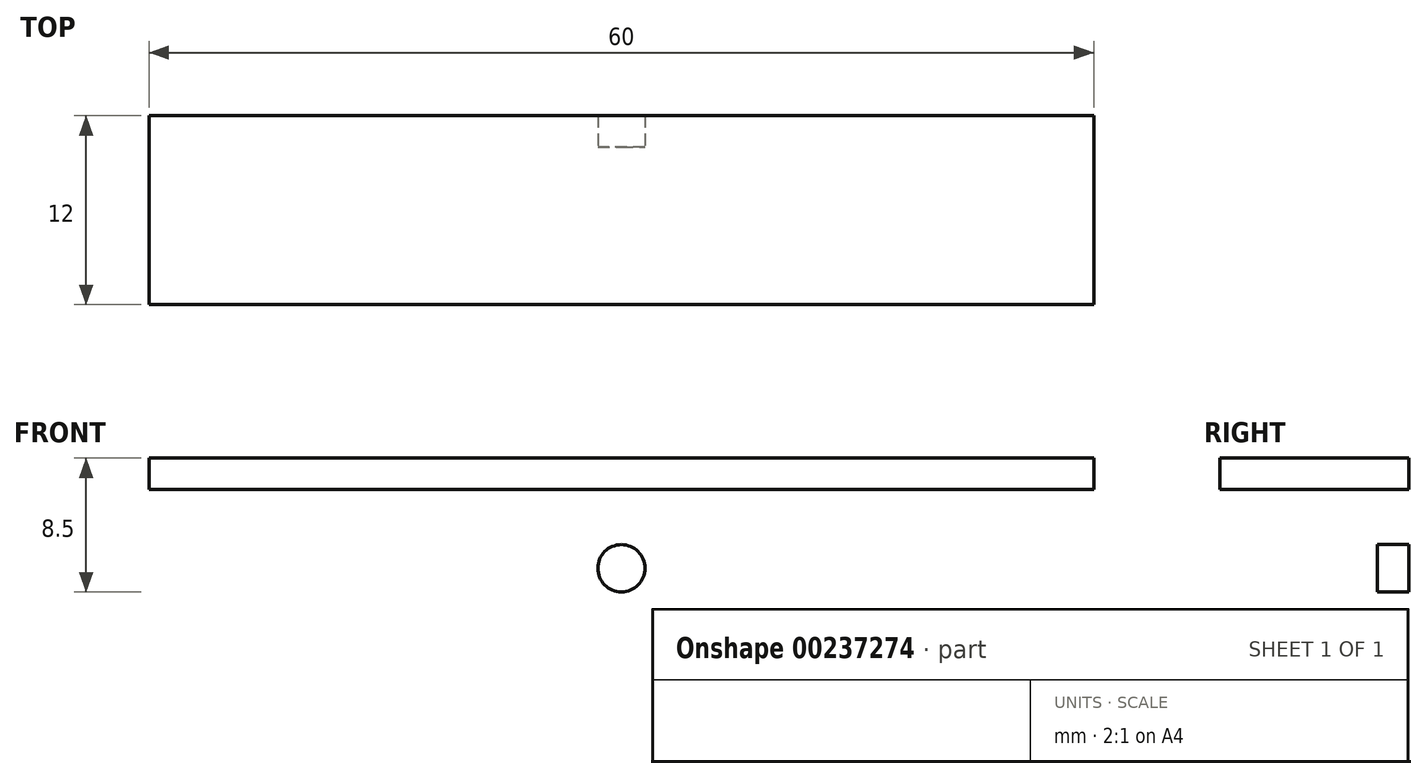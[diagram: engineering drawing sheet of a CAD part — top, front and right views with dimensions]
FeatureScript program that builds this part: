
annotation { "Feature Type Name" : "Feature", "Feature Type Description" : "" }
export const myFeature = defineFeature(function(context is Context, id is Id, definition is map)
    precondition{}
    {
        {
            var Q0;
            Q0=qCreatedBy(makeId("Front.planeOp"),FACE);
            var sketch = newSketch(context, id + "F0", { "sketchPlane" : qUnion([Q0])});
            skLineSegment(sketch, "E0.bottom", {"start": v(-30, 15) * mm, "end": v(30, 15) * mm});
            skLineSegment(sketch, "E0.top", {"start": v(-30, -15) * mm, "end": v(30, -15) * mm});
            skLineSegment(sketch, "E0.left", {"start": v(-30, 15) * mm, "end": v(-30, -15) * mm});
            skLineSegment(sketch, "E0.right", {"start": v(30, 15) * mm, "end": v(30, -15) * mm});
            skPoint(sketch, "E0.middle", {"position": v(0, 0) * mm});
            skSolve(sketch);
        }
        {
            var Q0;
            Q0=makeQuery(id+"F0.imprint","IMPRINT",FACE,{"disambiguationData":[TD([[makeQuery(id+"F0.imprint","IMPRINT",EDGE,{"derivedFrom":sQuery(id+"F0.wireOp",EDGE,"E0.bottom")}),-1.0]])]});
            extrude(context, id + "F1", {"entities" : qUnion([Q0]), "depth" : 2 * mm});
        }
        {
            var Q0;
            Q0=makeQuery(id+"F1.opExtrude","CAP_FACE",FACE,{"disambiguationData":[OSD([sQuery(id+"F0.wireOp",EDGE,"E0.bottom"),sQuery(id+"F0.wireOp",EDGE,"E0.top"),sQuery(id+"F0.wireOp",EDGE,"E0.left"),sQuery(id+"F0.wireOp",EDGE,"E0.right"),sQuery(id+"F0.wireOp",EDGE,"etlL4guk-orcU-iKfM-RefP-JZowgscgbXgj")])],"isStart":false});
            var sketch = newSketch(context, id + "F2", { "sketchPlane" : qUnion([Q0])});
            skLineSegment(sketch, "E1.bottom", {"start": v(-30, 15) * mm, "end": v(30, 15) * mm});
            skLineSegment(sketch, "E1.top", {"start": v(-30, 13) * mm, "end": v(30, 13) * mm});
            skLineSegment(sketch, "E1.left", {"start": v(-30, 15) * mm, "end": v(-30, 13) * mm});
            skLineSegment(sketch, "E1.right", {"start": v(30, 15) * mm, "end": v(30, 13) * mm});
            skSolve(sketch);
        }
        {
            var Q0;
            Q0 = qSketchRegion(id + "F2", true);
            extrude(context, id + "F3", {"entities" : qUnion([Q0]), "operationType" : NewBodyOperationType.ADD, "depth" : 10 * mm});
        }
        {
            var Q0;
            Q0=makeQuery(id+"F1.opExtrude","CAP_FACE",FACE,{"disambiguationData":[OSD([sQuery(id+"F0.wireOp",EDGE,"E0.bottom"),sQuery(id+"F0.wireOp",EDGE,"E0.top"),sQuery(id+"F0.wireOp",EDGE,"E0.left"),sQuery(id+"F0.wireOp",EDGE,"E0.right"),sQuery(id+"F0.wireOp",EDGE,"etlL4guk-orcU-iKfM-RefP-JZowgscgbXgj")])],"isStart":false});
            var sketch = newSketch(context, id + "F4", { "sketchPlane" : qUnion([Q0])});
            skLineSegment(sketch, "E2", {"start": v(-30, 8) * mm, "end": v(30, 8) * mm});
            skLineSegment(sketch, "E3.bottom", {"start": v(-26, 9) * mm, "end": v(-15, 9) * mm});
            skLineSegment(sketch, "E3.top", {"start": v(-26, 7) * mm, "end": v(-15, 7) * mm});
            skLineSegment(sketch, "E3.left", {"start": v(-26, 9) * mm, "end": v(-26, 7) * mm});
            skLineSegment(sketch, "E3.right", {"start": v(-15, 9) * mm, "end": v(-15, 7) * mm});
            skPoint(sketch, "E3.middle", {"position": v(-20.5, 8) * mm});
            skLineSegment(sketch, "E4.bottom", {"start": v(15, 9) * mm, "end": v(26, 9) * mm});
            skLineSegment(sketch, "E4.top", {"start": v(15, 7) * mm, "end": v(26, 7) * mm});
            skLineSegment(sketch, "E4.left", {"start": v(15, 9) * mm, "end": v(15, 7) * mm});
            skLineSegment(sketch, "E4.right", {"start": v(26, 9) * mm, "end": v(26, 7) * mm});
            skPoint(sketch, "E4.middle", {"position": v(20.5, 8) * mm});
            skCircle(sketch, "E5", {"center": v(0, 8) * mm, "radius": 1.5 * mm});
            skSolve(sketch);
        }
        {
            var Q0;
            {var subQ5=sQuery(id+"F4.wireOp",EDGE,"E4.bottom");Q0=makeQuery(id+"F4.imprint","IMPRINT",FACE,{"disambiguationData":[TD([[makeQuery(id+"F4.imprint","IMPRINT",EDGE,{"derivedFrom":subQ5}),-1.0]])]});}
            var Q1;
            {var subQ5=sQuery(id+"F4.wireOp",EDGE,"E4.top");Q1=makeQuery(id+"F4.imprint","IMPRINT",FACE,{"disambiguationData":[TD([[makeQuery(id+"F4.imprint","IMPRINT",EDGE,{"derivedFrom":subQ5}),1.0]])]});}
            var Q2;
            {var subQ0=sQuery(id+"F4.wireOp",EDGE,"E5");var subQ1=sQuery(id+"F4.wireOp",EDGE,"E2");var subQ2=makeQuery(id+"F4.imprint","INTERSECT",VERTEX,{"disambiguationData":[OD(0.0)],"derivedFrom":[subQ1,subQ0]});Q2=makeQuery(id+"F4.imprint","IMPRINT",FACE,{"disambiguationData":[TD([[makeQuery(id+"F4.imprint","IMPRINT",EDGE,{"disambiguationData":[TD([[subQ2,-1.0]])],"derivedFrom":subQ1}),-1.0]])]});}
            var Q3;
            {var subQ0=sQuery(id+"F4.wireOp",EDGE,"E5");var subQ1=sQuery(id+"F4.wireOp",EDGE,"E2");var subQ2=makeQuery(id+"F4.imprint","INTERSECT",VERTEX,{"disambiguationData":[OD(0.0)],"derivedFrom":[subQ1,subQ0]});Q3=makeQuery(id+"F4.imprint","IMPRINT",FACE,{"disambiguationData":[TD([[makeQuery(id+"F4.imprint","IMPRINT",EDGE,{"disambiguationData":[TD([[subQ2,-1.0]])],"derivedFrom":subQ1}),1.0]])]});}
            var Q4;
            {var subQ5=sQuery(id+"F4.wireOp",EDGE,"E3.bottom");Q4=makeQuery(id+"F4.imprint","IMPRINT",FACE,{"disambiguationData":[TD([[makeQuery(id+"F4.imprint","IMPRINT",EDGE,{"derivedFrom":subQ5}),-1.0]])]});}
            var Q5;
            {var subQ5=sQuery(id+"F4.wireOp",EDGE,"E3.top");Q5=makeQuery(id+"F4.imprint","IMPRINT",FACE,{"disambiguationData":[TD([[makeQuery(id+"F4.imprint","IMPRINT",EDGE,{"derivedFrom":subQ5}),1.0]])]});}
            extrude(context, id + "F5", {"entities" : qUnion([Q0, Q1, Q2, Q3, Q4, Q5]), "operationType" : NewBodyOperationType.REMOVE, "oppositeDirection" : true, "depth" : 3 * mm});
        }
        {
            var Q0;
            Q0=makeQuery(id+"F1.opExtrude","CAP_FACE",FACE,{"disambiguationData":[OSD([sQuery(id+"F0.wireOp",EDGE,"E0.bottom"),sQuery(id+"F0.wireOp",EDGE,"E0.top"),sQuery(id+"F0.wireOp",EDGE,"E0.left"),sQuery(id+"F0.wireOp",EDGE,"E0.right"),sQuery(id+"F0.wireOp",EDGE,"etlL4guk-orcU-iKfM-RefP-JZowgscgbXgj")])],"isStart":false});
            var sketch = newSketch(context, id + "F6", { "sketchPlane" : qUnion([Q0])});
            skLineSegment(sketch, "E6", {"start": v(-30, 3) * mm, "end": v(30, 3) * mm});
            skLineSegment(sketch, "E7.bottom", {"start": v(-26.03, 4) * mm, "end": v(-15.03, 4) * mm});
            skLineSegment(sketch, "E7.top", {"start": v(-26.03, 2) * mm, "end": v(-15.03, 2) * mm});
            skLineSegment(sketch, "E7.left", {"start": v(-26.03, 4) * mm, "end": v(-26.03, 2) * mm});
            skLineSegment(sketch, "E7.right", {"start": v(-15.03, 4) * mm, "end": v(-15.03, 2) * mm});
            skPoint(sketch, "E7.middle", {"position": v(-20.53, 3) * mm});
            skLineSegment(sketch, "E8.bottom", {"start": v(15.03, 4) * mm, "end": v(26.03, 4) * mm});
            skLineSegment(sketch, "E8.top", {"start": v(15.03, 2) * mm, "end": v(26.03, 2) * mm});
            skLineSegment(sketch, "E8.left", {"start": v(15.03, 4) * mm, "end": v(15.03, 2) * mm});
            skLineSegment(sketch, "E8.right", {"start": v(26.03, 4) * mm, "end": v(26.03, 2) * mm});
            skPoint(sketch, "E8.middle", {"position": v(20.53, 3) * mm});
            skCircle(sketch, "E9", {"center": v(0, 3) * mm, "radius": 1.5 * mm});
            skSolve(sketch);
        }
        {
            var Q0;
            Q0 = qSketchRegion(id + "F6", true);
            extrude(context, id + "F7", {"entities" : qUnion([Q0]), "operationType" : NewBodyOperationType.REMOVE, "oppositeDirection" : true, "depth" : 25 * mm});
        }
        {
            var Q0;
            Q0=makeQuery(id+"F1.opExtrude","CAP_FACE",FACE,{"disambiguationData":[OSD([sQuery(id+"F0.wireOp",EDGE,"E0.bottom"),sQuery(id+"F0.wireOp",EDGE,"E0.top"),sQuery(id+"F0.wireOp",EDGE,"E0.left"),sQuery(id+"F0.wireOp",EDGE,"E0.right")])],"isStart":false});
            var sketch = newSketch(context, id + "F8", { "sketchPlane" : qUnion([Q0])});
            skLineSegment(sketch, "E10", {"start": v(-30, -2) * mm, "end": v(30, -2) * mm});
            skLineSegment(sketch, "E11.bottom", {"start": v(-26.03, -1) * mm, "end": v(-15.03, -1) * mm});
            skLineSegment(sketch, "E11.top", {"start": v(-26.03, -3) * mm, "end": v(-15.03, -3) * mm});
            skLineSegment(sketch, "E11.left", {"start": v(-26.03, -1) * mm, "end": v(-26.03, -3) * mm});
            skLineSegment(sketch, "E11.right", {"start": v(-15.03, -1) * mm, "end": v(-15.03, -3) * mm});
            skPoint(sketch, "E11.middle", {"position": v(-20.53, -2) * mm});
            skLineSegment(sketch, "E12.bottom", {"start": v(15.03, -1) * mm, "end": v(26.03, -1) * mm});
            skLineSegment(sketch, "E12.top", {"start": v(15.03, -3) * mm, "end": v(26.03, -3) * mm});
            skLineSegment(sketch, "E12.left", {"start": v(15.03, -1) * mm, "end": v(15.03, -3) * mm});
            skLineSegment(sketch, "E12.right", {"start": v(26.03, -1) * mm, "end": v(26.03, -3) * mm});
            skPoint(sketch, "E12.middle", {"position": v(20.53, -2) * mm});
            skCircle(sketch, "E13", {"center": v(0, -2) * mm, "radius": 1.5 * mm});
            skSolve(sketch);
        }
        {
            var Q0;
            Q0 = qSketchRegion(id + "F8", true);
            extrude(context, id + "F9", {"entities" : qUnion([Q0]), "operationType" : NewBodyOperationType.REMOVE, "oppositeDirection" : true, "depth" : 25 * mm});
        }
        {
            var Q0;
            Q0=makeQuery(id+"F1.opExtrude","CAP_FACE",FACE,{"disambiguationData":[OSD([sQuery(id+"F0.wireOp",EDGE,"E0.bottom"),sQuery(id+"F0.wireOp",EDGE,"E0.top"),sQuery(id+"F0.wireOp",EDGE,"E0.left"),sQuery(id+"F0.wireOp",EDGE,"E0.right")])],"isStart":false});
            var sketch = newSketch(context, id + "F10", { "sketchPlane" : qUnion([Q0])});
            skLineSegment(sketch, "E14", {"start": v(-30, -7) * mm, "end": v(30, -7) * mm});
            skLineSegment(sketch, "E15.bottom", {"start": v(-26.03, -6) * mm, "end": v(-15.03, -6) * mm});
            skLineSegment(sketch, "E15.top", {"start": v(-26.03, -8) * mm, "end": v(-15.03, -8) * mm});
            skLineSegment(sketch, "E15.left", {"start": v(-26.03, -6) * mm, "end": v(-26.03, -8) * mm});
            skLineSegment(sketch, "E15.right", {"start": v(-15.03, -6) * mm, "end": v(-15.03, -8) * mm});
            skPoint(sketch, "E15.middle", {"position": v(-20.53, -7) * mm});
            skLineSegment(sketch, "E16.bottom", {"start": v(15.03, -6) * mm, "end": v(26.03, -6) * mm});
            skLineSegment(sketch, "E16.top", {"start": v(15.03, -8) * mm, "end": v(26.03, -8) * mm});
            skLineSegment(sketch, "E16.left", {"start": v(15.03, -6) * mm, "end": v(15.03, -8) * mm});
            skLineSegment(sketch, "E16.right", {"start": v(26.03, -6) * mm, "end": v(26.03, -8) * mm});
            skPoint(sketch, "E16.middle", {"position": v(20.53, -7) * mm});
            skCircle(sketch, "E17", {"center": v(0, -7) * mm, "radius": 1.5 * mm});
            skSolve(sketch);
        }
        {
            var Q0;
            Q0 = qSketchRegion(id + "F10", true);
            extrude(context, id + "F11", {"entities" : qUnion([Q0]), "operationType" : NewBodyOperationType.REMOVE, "oppositeDirection" : true, "depth" : 25 * mm});
        }
        {
            var Q0;
            Q0=makeQuery(id+"F1.opExtrude","CAP_FACE",FACE,{"disambiguationData":[OSD([sQuery(id+"F0.wireOp",EDGE,"E0.bottom"),sQuery(id+"F0.wireOp",EDGE,"E0.top"),sQuery(id+"F0.wireOp",EDGE,"E0.left"),sQuery(id+"F0.wireOp",EDGE,"E0.right")])],"isStart":false});
            var sketch = newSketch(context, id + "F12", { "sketchPlane" : qUnion([Q0])});
            skLineSegment(sketch, "E18", {"start": v(-30, -12) * mm, "end": v(30, -12) * mm});
            skLineSegment(sketch, "E19.bottom", {"start": v(-26.03, -11) * mm, "end": v(-15.03, -11) * mm});
            skLineSegment(sketch, "E19.top", {"start": v(-26.03, -13) * mm, "end": v(-15.03, -13) * mm});
            skLineSegment(sketch, "E19.left", {"start": v(-26.03, -11) * mm, "end": v(-26.03, -13) * mm});
            skLineSegment(sketch, "E19.right", {"start": v(-15.03, -11) * mm, "end": v(-15.03, -13) * mm});
            skPoint(sketch, "E19.middle", {"position": v(-20.53, -12) * mm});
            skLineSegment(sketch, "E20.bottom", {"start": v(15.03, -11) * mm, "end": v(26.03, -11) * mm});
            skLineSegment(sketch, "E20.top", {"start": v(15.03, -13) * mm, "end": v(26.03, -13) * mm});
            skLineSegment(sketch, "E20.left", {"start": v(15.03, -11) * mm, "end": v(15.03, -13) * mm});
            skLineSegment(sketch, "E20.right", {"start": v(26.03, -11) * mm, "end": v(26.03, -13) * mm});
            skPoint(sketch, "E20.middle", {"position": v(20.53, -12) * mm});
            skCircle(sketch, "E21", {"center": v(0, -12) * mm, "radius": 1.5 * mm});
            skSolve(sketch);
        }
        {
            var Q0;
            Q0 = qSketchRegion(id + "F12", true);
            extrude(context, id + "F13", {"entities" : qUnion([Q0]), "operationType" : NewBodyOperationType.REMOVE, "oppositeDirection" : true, "depth" : 25 * mm});
        }
        {
            var Q0;
            Q0=makeQuery(id+"F1.opExtrude","CAP_FACE",FACE,{"disambiguationData":[OSD([sQuery(id+"F0.wireOp",EDGE,"E0.bottom"),sQuery(id+"F0.wireOp",EDGE,"E0.top"),sQuery(id+"F0.wireOp",EDGE,"E0.left"),sQuery(id+"F0.wireOp",EDGE,"E0.right")])],"isStart":false});
            var sketch = newSketch(context, id + "F14", { "sketchPlane" : qUnion([Q0])});
            skText(sketch, "E22", { "text": "5", "fontName": "OpenSans-Bold.ttf"});
            const initialGuessF14  = {"E22": [0.00423, 0.00641, 1, 0, 0.00403]};
            skSetInitialGuess(sketch, initialGuessF14);
            skSolve(sketch);
        }
        {
            var Q0;
            Q0 = qSketchRegion(id + "F14", true);
            extrude(context, id + "F15", {"entities" : qUnion([Q0]), "operationType" : NewBodyOperationType.REMOVE, "oppositeDirection" : true, "depth" : 1 * mm});
        }
        {
            var Q0;
            Q0=makeQuery(id+"F1.opExtrude","CAP_FACE",FACE,{"disambiguationData":[OSD([sQuery(id+"F0.wireOp",EDGE,"E0.bottom"),sQuery(id+"F0.wireOp",EDGE,"E0.top"),sQuery(id+"F0.wireOp",EDGE,"E0.left"),sQuery(id+"F0.wireOp",EDGE,"E0.right")])],"isStart":false});
            var sketch = newSketch(context, id + "F16", { "sketchPlane" : qUnion([Q0])});
            skText(sketch, "E23", { "text": "10", "fontName": "OpenSans-Bold.ttf"});
            const initialGuessF16  = {"E23": [-0.01024, 0.00126, 1, 0, 0.00348]};
            skSetInitialGuess(sketch, initialGuessF16);
            skSolve(sketch);
        }
        {
            var Q0;
            Q0 = qSketchRegion(id + "F16", true);
            extrude(context, id + "F17", {"entities" : qUnion([Q0]), "operationType" : NewBodyOperationType.REMOVE, "oppositeDirection" : true, "depth" : 1 * mm});
        }
        {
            var Q0;
            {var subQ0=sQuery(id+"F0.wireOp",EDGE,"E0.left");var subQ1=sQuery(id+"F0.wireOp",EDGE,"E0.top");var subQ2=sQuery(id+"F0.wireOp",EDGE,"E0.right");Q0=makeQuery(id+"F17.boolean.opBoolean","SPLIT",FACE,{"disambiguationData":[TD([makeQuery(id+"F1.opExtrude","SWEPT_FACE",FACE,{"disambiguationData":[OSD([subQ1])]})])],"derivedFrom":makeQuery(id+"F1.opExtrude","CAP_FACE",FACE,{"disambiguationData":[OSD([sQuery(id+"F0.wireOp",EDGE,"E0.bottom"),subQ1,subQ0,subQ2])],"isStart":false})});}
            var sketch = newSketch(context, id + "F18", { "sketchPlane" : qUnion([Q0])});
            skText(sketch, "E24", { "text": "15", "fontName": "OpenSans-Bold.ttf"});
            const initialGuessF18  = {"E24": [0.0052, -0.0036, 1, 0, 0.0036]};
            skSetInitialGuess(sketch, initialGuessF18);
            skSolve(sketch);
        }
        {
            var Q0;
            Q0 = qSketchRegion(id + "F18", true);
            extrude(context, id + "F19", {"entities" : qUnion([Q0]), "operationType" : NewBodyOperationType.REMOVE, "oppositeDirection" : true, "depth" : 1 * mm});
        }
        {
            var Q0;
            {var subQ0=sQuery(id+"F0.wireOp",EDGE,"E0.left");var subQ1=sQuery(id+"F0.wireOp",EDGE,"E0.top");var subQ2=sQuery(id+"F0.wireOp",EDGE,"E0.right");Q0=makeQuery(id+"F17.boolean.opBoolean","SPLIT",FACE,{"disambiguationData":[TD([makeQuery(id+"F1.opExtrude","SWEPT_FACE",FACE,{"disambiguationData":[OSD([subQ1])]})])],"derivedFrom":makeQuery(id+"F1.opExtrude","CAP_FACE",FACE,{"disambiguationData":[OSD([sQuery(id+"F0.wireOp",EDGE,"E0.bottom"),subQ1,subQ0,subQ2])],"isStart":false})});}
            var sketch = newSketch(context, id + "F20", { "sketchPlane" : qUnion([Q0])});
            skText(sketch, "E25", { "text": "20", "fontName": "OpenSans-Bold.ttf"});
            const initialGuessF20  = {"E25": [-0.0101, -0.00875, 1, 0, 0.0039]};
            skSetInitialGuess(sketch, initialGuessF20);
            skSolve(sketch);
        }
        {
            var Q0;
            Q0 = qSketchRegion(id + "F20", true);
            extrude(context, id + "F21", {"entities" : qUnion([Q0]), "operationType" : NewBodyOperationType.REMOVE, "oppositeDirection" : true, "depth" : 1 * mm});
        }
        {
            var Q0;
            {var subQ54=sQuery(id+"F0.wireOp",EDGE,"E0.right");var subQ63=sQuery(id+"F0.wireOp",EDGE,"E0.top");var subQ64=makeQuery(id+"F1.opExtrude","SWEPT_FACE",FACE,{"disambiguationData":[OSD([subQ63])]});var subQ67=sQuery(id+"F0.wireOp",EDGE,"E0.left");Q0=makeQuery(id+"F21.boolean.opBoolean","SPLIT",FACE,{"disambiguationData":[TD([subQ64])],"derivedFrom":makeQuery(id+"F17.boolean.opBoolean","SPLIT",FACE,{"disambiguationData":[TD([subQ64])],"derivedFrom":makeQuery(id+"F1.opExtrude","CAP_FACE",FACE,{"disambiguationData":[OSD([sQuery(id+"F0.wireOp",EDGE,"E0.bottom"),subQ63,subQ67,subQ54])],"isStart":false})})});}
            var sketch = newSketch(context, id + "F22", { "sketchPlane" : qUnion([Q0])});
            skText(sketch, "E26", { "text": "25", "fontName": "OpenSans-Bold.ttf"});
            const initialGuessF22  = {"E26": [0.00576, -0.0132, 1, 0, 0.00348]};
            skSetInitialGuess(sketch, initialGuessF22);
            skSolve(sketch);
        }
        {
            var Q0;
            Q0 = qSketchRegion(id + "F22", true);
            extrude(context, id + "F23", {"entities" : qUnion([Q0]), "operationType" : NewBodyOperationType.REMOVE, "oppositeDirection" : true, "depth" : 1 * mm});
        }
    });
